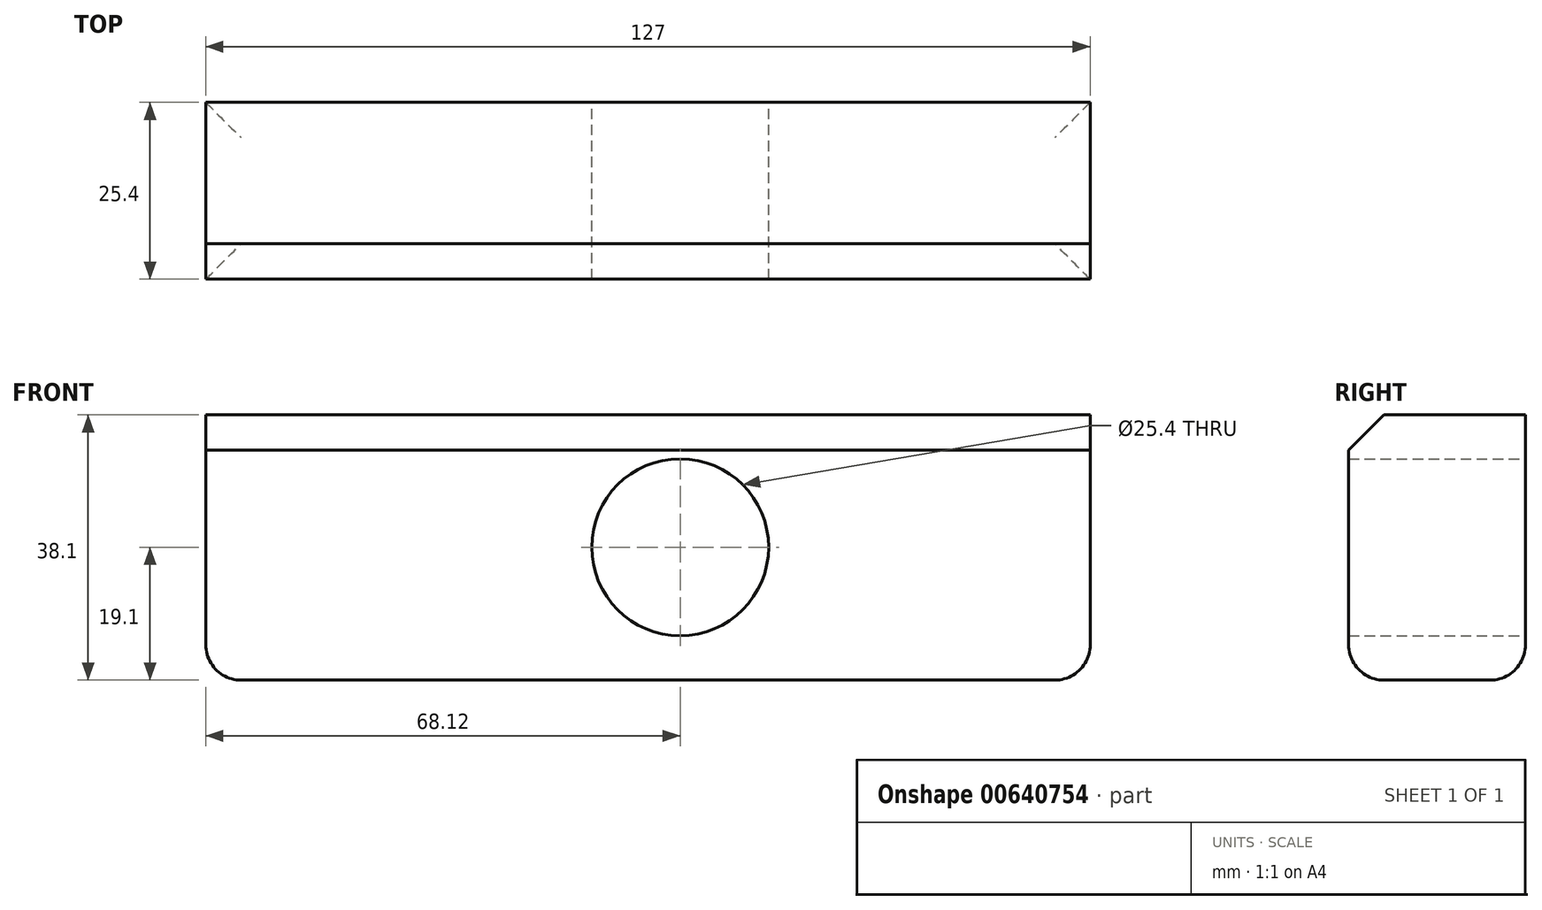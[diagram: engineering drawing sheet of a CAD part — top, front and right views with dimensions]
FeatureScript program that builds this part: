
annotation { "Feature Type Name" : "Feature", "Feature Type Description" : "" }
export const myFeature = defineFeature(function(context is Context, id is Id, definition is map)
    precondition{}
    {
        {
            var Q0;
            Q0=qCreatedBy(makeId("Front.planeOp"),FACE);
            var sketch = newSketch(context, id + "F0", { "sketchPlane" : qUnion([Q0])});
            skCircle(sketch, "E0", {"center": v(0, 0) * mm, "radius": 12.7 * mm});
            skLineSegment(sketch, "E1.bottom", {"start": v(58.88, 19) * mm, "end": v(-68.12, 19) * mm});
            skLineSegment(sketch, "E1.top", {"start": v(58.88, -19.1) * mm, "end": v(-68.12, -19.1) * mm});
            skLineSegment(sketch, "E1.left", {"start": v(58.88, 19) * mm, "end": v(58.88, -19.1) * mm});
            skLineSegment(sketch, "E1.right", {"start": v(-68.12, 19) * mm, "end": v(-68.12, -19.1) * mm});
            skSolve(sketch);
        }
        {
            var Q0;
            Q0 = qSketchRegion(id + "F0", true);
            extrude(context, id + "F1", {"entities" : qUnion([Q0]), "depth" : 25.4 * mm, "offsetDistance" : 25 * mm});
        }
        {
            var Q0;
            Q0=makeQuery(id+"F1.opExtrude","CAP_EDGE",EDGE,{"disambiguationData":[OSD([sQuery(id+"F0.wireOp",EDGE,"E1.bottom")])],"isStart":false});
            chamfer(context, id + "F2", {"entities" : qUnion([Q0]), "width" : 5.08 * mm, "tangentPropagation" : true});
        }
        {
            var Q0;
            Q0=makeQuery(id+"F1.opExtrude","SWEPT_FACE",FACE,{"disambiguationData":[OSD([sQuery(id+"F0.wireOp",EDGE,"E1.top")])]});
            fillet(context, id + "F3", {"entities" : qUnion([Q0]), "radius" : 5.08 * mm, "tangentPropagation" : true, "allowEdgeOverflow" : false});
        }
    });
